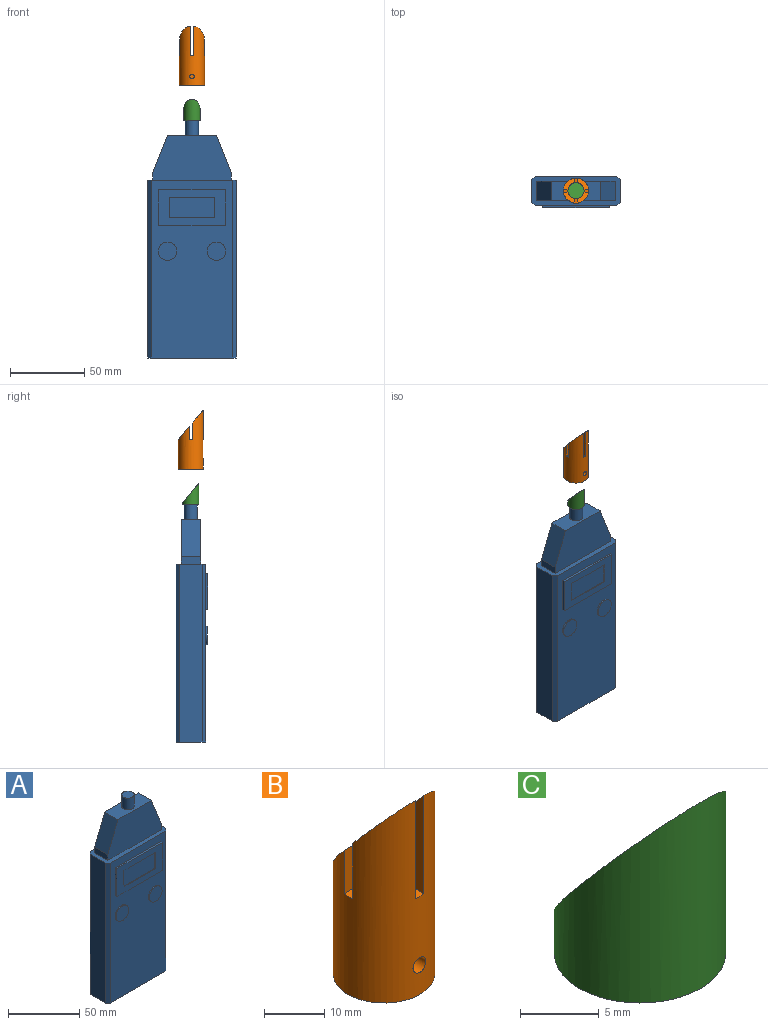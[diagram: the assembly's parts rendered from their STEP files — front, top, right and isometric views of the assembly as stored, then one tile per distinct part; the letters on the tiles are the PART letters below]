
ASSEMBLY  parts=3 mates=2
PART A: 33 faces, bbox 60x21.5x160 mm
  f0: plane 45x24mm, normal (0,-1,0), area 646mm2, adj f16,f17,f18,f19,f20,f21,f22,f23
  f1: plane 120x55mm, normal (0,-1,0), area 5274.6mm2, adj f3,f5,f16,f17,f18,f19,f25,f27
  f2: plane 120x15mm, normal (-1,0,0), area 1800mm2, adj f3,f5,f29,f32
  f3: plane 60x20mm, normal (0,0,-1), area 1187.5mm2, adj f1,f2,f4,f6,f29,f30,f31,f32
  f4: plane 120x15mm, normal (1,0,0), area 1800mm2, adj f3,f5,f30,f31
  f5: plane 60x20mm, normal (0,0,1), area 498.5mm2, adj f1,f2,f4,f6,f7,f8,f9,f10
  f6: plane 120x55mm, normal (0,1,0), area 6600mm2, adj f3,f5,f29,f30
  f7: plane 13x5mm, normal (-1,0,0), area 65mm2, adj f5,f8,f10,f13
  f8: plane 53x30mm, normal (0,-1,0), area 1340mm2, adj f5,f7,f9,f11,f12,f13
  f9: plane 13x5mm, normal (1,0,0), area 65mm2, adj f5,f8,f10,f12
  f10: plane 53x30mm, normal (0,1,0), area 1340mm2, adj f5,f7,f9,f11,f12,f13
  f11: plane 33x13mm, normal (0,0,1), area 368.2mm2, adj f8,f10,f12,f13,f14
  f12: plane 25x13mm, normal (0.93,0,0.37), area 350mm2, adj f8,f9,f10,f11
  f13: plane 25x13mm, normal (-0.93,0,0.37), area 350mm2, adj f7,f8,f10,f11
  f14: cylinder r=4.4mm len=10mm, axis (0,0,-1), area 276.5mm2, adj f11,f15
  f15: plane 8.8x8.8mm, normal (0,0,1), area 60.8mm2, adj f14
  f16: plane 45x1.5mm, normal (0,0,1), area 67.5mm2, adj f0,f1,f17,f19
  f17: plane 24x1.5mm, normal (-1,0,0), area 36mm2, adj f0,f1,f16,f18
  f18: plane 45x1.5mm, normal (0,0,-1), area 67.5mm2, adj f0,f1,f17,f19
  f19: plane 24x1.5mm, normal (1,0,0), area 36mm2, adj f0,f1,f16,f18
  f20: plane 14x0.5mm, normal (1,0,0), area 7mm2, adj f0,f21,f23,f24
  f21: plane 31x0.5mm, normal (0,0,1), area 15.5mm2, adj f0,f20,f22,f24
  f22: plane 14x0.5mm, normal (-1,0,0), area 7mm2, adj f0,f21,f23,f24
  f23: plane 31x0.5mm, normal (0,0,-1), area 15.5mm2, adj f0,f20,f22,f24
  f24: plane 31x14mm, normal (0,-1,0), area 434mm2, adj f20,f21,f22,f23
  f25: cylinder r=6.25mm len=12.5mm, axis (0,1,0), area 39.3mm2, adj f1,f26
  f26: plane 12.5x12.5mm, normal (0,-1,0), area 122.7mm2, adj f25
  f27: cylinder r=6.25mm len=12.5mm, axis (0,1,0), area 39.3mm2, adj f1,f28
  f28: plane 12.5x12.5mm, normal (0,-1,0), area 122.7mm2, adj f27
  f29: plane 120x2.5mm, normal (-0.71,0.71,0), area 424.3mm2, adj f2,f3,f5,f6
  f30: plane 120x2.5mm, normal (0.71,0.71,0), area 424.3mm2, adj f3,f4,f5,f6
  f31: plane 120x2.5mm, normal (0.71,-0.71,0), area 424.3mm2, adj f1,f3,f4,f5
  f32: plane 120x2.5mm, normal (-0.71,-0.71,0), area 424.3mm2, adj f1,f2,f3,f5
PART B: 21 faces, bbox 18.6x18.5x41.6 mm
  f0: cylinder r=5.45mm len=36.39mm, axis (0,0,-1), area 939.7mm2, adj f2,f3,f4,f5,f6,f7,f8,f9
  f1: cylinder r=8.45mm len=40mm, axis (0,0,-1), area 1505.5mm2, adj f2,f3,f4,f5,f6,f7,f8,f12
  f2: plane 16.9x16.9mm, normal (0,0,-1), area 131mm2, adj f0,f1
  f3: plane 20.01x3.04mm, normal (1,0,0), area 55.1mm2, adj f0,f1,f5,f19
  f4: plane 20.01x3.04mm, normal (-1,0,0), area 55.1mm2, adj f0,f1,f5,f16
  f5: plane 3.12x2.01mm, normal (0,0,1), area 6mm2, adj f0,f1,f3,f4
  f6: plane 8.82x3.04mm, normal (0,-1,0), area 26.7mm2, adj f0,f1,f8,f18
  f7: plane 11.2x3.04mm, normal (0,1,0), area 33.9mm2, adj f0,f1,f8,f19
  f8: plane 3.12x2.01mm, normal (0,0,1), area 6mm2, adj f0,f1,f6,f7
  f9: plane 3.62x3.04mm, normal (-1,0,0), area 5.5mm2, adj f0,f11,f15
  f10: plane 3.62x3.03mm, normal (1,0,0), area 5.5mm2, adj f0,f11,f18
  f11: plane 3.04x2mm, normal (0,0,1), area 5.9mm2, adj f0,f9,f10,f17
  f12: plane 11.2x3.04mm, normal (0,1,0), area 33.9mm2, adj f0,f1,f14,f16
  f13: plane 8.82x3.04mm, normal (0,-1,0), area 26.7mm2, adj f0,f1,f14,f15
  f14: plane 3.12x2.01mm, normal (0,0,1), area 6mm2, adj f0,f1,f12,f13
  f15: plane 10.43x9.02mm, normal (0,0.77,0.64), area 41.6mm2, adj f0,f1,f9,f13
  f16: plane 10.43x9.02mm, normal (0,0.77,0.64), area 41.6mm2, adj f0,f1,f4,f12
  f17: plane 2.13x0.21mm, normal (0,0.77,0.64), area 0.1mm2, adj f1,f11
  f18: plane 10.43x9.02mm, normal (0,0.77,0.64), area 41.6mm2, adj f0,f1,f6,f10
  f19: plane 10.43x9.02mm, normal (0,0.77,0.64), area 41.6mm2, adj f0,f1,f3,f7
  f20: cylinder r=1.5mm len=3mm, axis (0,-1,0), area 28.3mm2, adj f0,f1
PART C: 3 faces, bbox 10.9x10.9x14.6 mm
  f0: cylinder r=5.45mm len=14.59mm, axis (0,0,-1), area 274.1mm2, adj f1,f2
  f1: plane 10.9x10.9mm, normal (0,0,-1), area 93.3mm2, adj f0
  f2: plane 12.99x10.9mm, normal (0,0.77,0.64), area 145.2mm2, adj f0
PLACE A t=(11.79,58.64,-19.13)mm
PLACE B t=(41.79,68.64,164.9)mm
PLACE C t=(11.79,58.64,-19.13)mm
MATE cylindrical C.f0 <-> A.f14  axis (0,0,-1) through (41.79,68.64,140.87)mm
MATE cylindrical B.f1 <-> A.f14  axis (0,0,-1) through (41.79,68.64,164.9)mm
